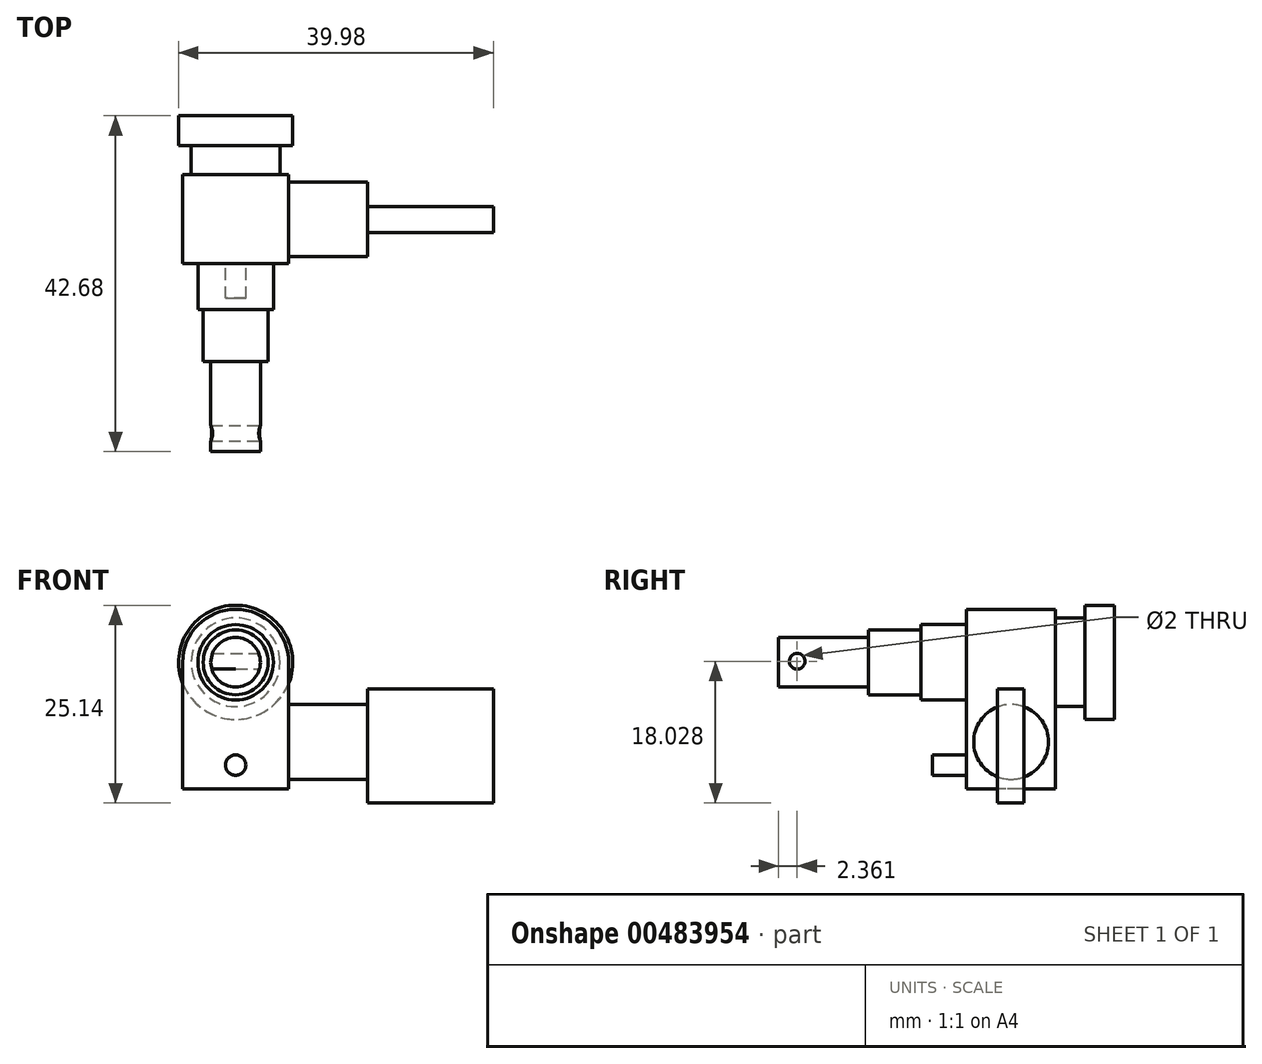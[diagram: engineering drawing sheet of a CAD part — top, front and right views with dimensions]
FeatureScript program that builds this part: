
annotation { "Feature Type Name" : "Feature", "Feature Type Description" : "" }
export const myFeature = defineFeature(function(context is Context, id is Id, definition is map)
    precondition{}
    {
        {
            var Q0;
            Q0=qCreatedBy(makeId("Front.planeOp"),FACE);
            var sketch = newSketch(context, id + "F0", { "sketchPlane" : qUnion([Q0])});
            skLineSegment(sketch, "E0", {"start": v(-6.73, 11.53) * mm, "end": v(-6.73, -4.58) * mm});
            skLineSegment(sketch, "E1", {"start": v(-6.73, -4.58) * mm, "end": v(6.73, -4.58) * mm});
            skLineSegment(sketch, "E2", {"start": v(6.73, -4.58) * mm, "end": v(6.73, 11.53) * mm});
            skArc(sketch, "E3", {"start": v(6.73, 11.53) * mm, "mid": v(0, 18.26) * mm, "end": v(-6.73, 11.53) * mm});
            skSolve(sketch);
        }
        {
            var Q0;
            Q0 = qSketchRegion(id + "F0", true);
            extrude(context, id + "F1", {"entities" : qUnion([Q0]), "oppositeDirection" : true, "depth" : 11.3 * mm});
        }
        {
            var Q0;
            Q0=makeQuery(id+"F1.opExtrude","CAP_FACE",FACE,{"disambiguationData":[OSD([sQuery(id+"F0.wireOp",EDGE,"E0"),sQuery(id+"F0.wireOp",EDGE,"E1"),sQuery(id+"F0.wireOp",EDGE,"E2"),sQuery(id+"F0.wireOp",EDGE,"E3")])],"isStart":true});
            var sketch = newSketch(context, id + "F2", { "sketchPlane" : qUnion([Q0])});
            skCircle(sketch, "E4", {"center": v(0, 11.53) * mm, "radius": 4.8 * mm});
            skSolve(sketch);
        }
        {
            var Q0;
            Q0 = qSketchRegion(id + "F2", true);
            extrude(context, id + "F3", {"entities" : qUnion([Q0]), "operationType" : NewBodyOperationType.ADD, "depth" : 5.8 * mm});
        }
        {
            var Q0;
            Q0=makeQuery(id+"F1.opExtrude","CAP_FACE",FACE,{"disambiguationData":[OSD([sQuery(id+"F0.wireOp",EDGE,"E0"),sQuery(id+"F0.wireOp",EDGE,"E1"),sQuery(id+"F0.wireOp",EDGE,"E2"),sQuery(id+"F0.wireOp",EDGE,"E3")])],"isStart":true});
            var sketch = newSketch(context, id + "F4", { "sketchPlane" : qUnion([Q0])});
            skCircle(sketch, "E5", {"center": v(0, 11.53) * mm, "radius": 4.13 * mm});
            skSolve(sketch);
        }
        {
            var Q0;
            Q0 = qSketchRegion(id + "F4", true);
            extrude(context, id + "F5", {"entities" : qUnion([Q0]), "operationType" : NewBodyOperationType.ADD, "depth" : 12.45 * mm});
        }
        {
            var Q0;
            Q0=makeQuery(id+"F4.imprint","IMPRINT",FACE,{"disambiguationData":[TD([[makeQuery(id+"F4.imprint","IMPRINT",EDGE,{"derivedFrom":makeQuery(id+"F1.opExtrude","CAP_EDGE",EDGE,{"disambiguationData":[OSD([sQuery(id+"F0.wireOp",EDGE,"E0")])],"isStart":true})}),1.0]])]});
            var sketch = newSketch(context, id + "F6", { "sketchPlane" : qUnion([Q0])});
            skCircle(sketch, "E6", {"center": v(0, 11.53) * mm, "radius": 3.15 * mm});
            skSolve(sketch);
        }
        {
            var Q0;
            Q0 = qSketchRegion(id + "F6", true);
            extrude(context, id + "F7", {"entities" : qUnion([Q0]), "operationType" : NewBodyOperationType.ADD, "depth" : 23.88 * mm});
        }
        {
            var Q0;
            Q0=qCreatedBy(makeId("Right.planeOp"),FACE);
            var sketch = newSketch(context, id + "F8", { "sketchPlane" : qUnion([Q0])});
            skCircle(sketch, "E7", {"center": v(-21.52, 11.67) * mm, "radius": 1 * mm});
            skSolve(sketch);
        }
        {
            var Q0;
            Q0 = qSketchRegion(id + "F8", true);
            extrude(context, id + "F9", {"entities" : qUnion([Q0]), "operationType" : NewBodyOperationType.REMOVE, "endBound" : BoundingType.THROUGH_ALL, "oppositeDirection" : true, "depth" : 25 * mm, "hasSecondDirection" : true, "secondDirectionBound" : SecondDirectionBoundingType.THROUGH_ALL, "secondDirectionOppositeDirection" : false, "secondDirectionDepth" : 25 * mm});
        }
        {
            var Q0;
            Q0=makeQuery(id+"F1.opExtrude","CAP_FACE",FACE,{"disambiguationData":[OSD([sQuery(id+"F0.wireOp",EDGE,"E0"),sQuery(id+"F0.wireOp",EDGE,"E1"),sQuery(id+"F0.wireOp",EDGE,"E2"),sQuery(id+"F0.wireOp",EDGE,"E3")])],"isStart":false});
            var sketch = newSketch(context, id + "F10", { "sketchPlane" : qUnion([Q0])});
            skCircle(sketch, "E8", {"center": v(0, 11.53) * mm, "radius": 5.64 * mm});
            skSolve(sketch);
        }
        {
            var Q0;
            Q0 = qSketchRegion(id + "F10", true);
            extrude(context, id + "F11", {"entities" : qUnion([Q0]), "operationType" : NewBodyOperationType.ADD, "depth" : 3.7 * mm});
        }
        {
            var Q0;
            Q0=makeQuery(id+"F11.opExtrude","CAP_FACE",FACE,{"disambiguationData":[OSD([sQuery(id+"F10.wireOp",EDGE,"E8")])],"isStart":false});
            var sketch = newSketch(context, id + "F12", { "sketchPlane" : qUnion([Q0])});
            skCircle(sketch, "E9", {"center": v(0, 11.53) * mm, "radius": 7.25 * mm});
            skSolve(sketch);
        }
        {
            var Q0;
            Q0=makeQuery(id+"F12.imprint","IMPRINT",FACE,{"disambiguationData":[TD([[makeQuery(id+"F12.imprint","IMPRINT",EDGE,{"derivedFrom":sQuery(id+"F12.wireOp",EDGE,"E9")}),1.0]])]});
            var Q1;
            Q1=makeQuery(id+"F12.imprint","IMPRINT",FACE,{"disambiguationData":[TD([[makeQuery(id+"F12.imprint","IMPRINT",EDGE,{"derivedFrom":makeQuery(id+"F11.opExtrude","CAP_EDGE",EDGE,{"disambiguationData":[OSD([sQuery(id+"F10.wireOp",EDGE,"E8")])],"isStart":false})}),1.0]])]});
            extrude(context, id + "F13", {"entities" : qUnion([Q0, Q1]), "operationType" : NewBodyOperationType.ADD, "depth" : 3.8 * mm});
        }
        {
            var Q0;
            Q0=makeQuery(id+"F1.opExtrude","SWEPT_FACE",FACE,{"disambiguationData":[OSD([sQuery(id+"F0.wireOp",EDGE,"E2")])]});
            var sketch = newSketch(context, id + "F14", { "sketchPlane" : qUnion([Q0])});
            skLineSegment(sketch, "E10", {"start": v(5.65, -4.58) * mm, "end": v(5.65, 7.42) * mm, "construction": true});
            skCircle(sketch, "E11", {"center": v(5.65, 1.42) * mm, "radius": 4.75 * mm});
            skSolve(sketch);
        }
        {
            var Q0;
            Q0=makeQuery(id+"F14.imprint","IMPRINT",FACE,{"disambiguationData":[TD([[makeQuery(id+"F14.imprint","IMPRINT",EDGE,{"derivedFrom":sQuery(id+"F14.wireOp",EDGE,"E11")}),1.0]])]});
            extrude(context, id + "F15", {"entities" : qUnion([Q0]), "operationType" : NewBodyOperationType.ADD, "depth" : 10 * mm});
        }
        {
            var Q0;
            Q0=makeQuery(id+"F15.opExtrude","CAP_FACE",FACE,{"disambiguationData":[OSD([sQuery(id+"F14.wireOp",EDGE,"E11")])],"isStart":false});
            var sketch = newSketch(context, id + "F16", { "sketchPlane" : qUnion([Q0])});
            skLineSegment(sketch, "E12.bottom", {"start": v(3.94, 8.13) * mm, "end": v(7.3, 8.13) * mm});
            skLineSegment(sketch, "E12.top", {"start": v(3.94, -6.36) * mm, "end": v(7.3, -6.36) * mm});
            skLineSegment(sketch, "E12.left", {"start": v(3.94, 8.13) * mm, "end": v(3.94, -6.36) * mm});
            skLineSegment(sketch, "E12.right", {"start": v(7.3, 8.13) * mm, "end": v(7.3, -6.36) * mm});
            skSolve(sketch);
        }
        {
            var Q0;
            Q0 = qSketchRegion(id + "F16", true);
            extrude(context, id + "F17", {"entities" : qUnion([Q0]), "operationType" : NewBodyOperationType.ADD, "depth" : 16 * mm});
        }
        {
            var Q0;
            Q0=makeQuery(id+"F4.imprint","IMPRINT",FACE,{"disambiguationData":[TD([[makeQuery(id+"F4.imprint","IMPRINT",EDGE,{"derivedFrom":makeQuery(id+"F1.opExtrude","CAP_EDGE",EDGE,{"disambiguationData":[OSD([sQuery(id+"F0.wireOp",EDGE,"E0")])],"isStart":true})}),1.0]])]});
            var sketch = newSketch(context, id + "F18", { "sketchPlane" : qUnion([Q0])});
            skCircle(sketch, "E13", {"center": v(0, -1.53) * mm, "radius": 1.3 * mm});
            skSolve(sketch);
        }
        {
            var Q0;
            Q0 = qSketchRegion(id + "F18", true);
            var Q1;
            Q1=sQuery(id+"F18.wireOp",EDGE,"E13");
            extrude(context, id + "F19", {"entities" : qUnion([Q0]), "operationType" : NewBodyOperationType.ADD, "surfaceEntities" : qUnion([Q1]), "depth" : 4.37 * mm});
        }
    });
